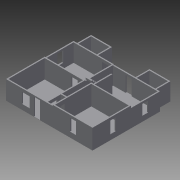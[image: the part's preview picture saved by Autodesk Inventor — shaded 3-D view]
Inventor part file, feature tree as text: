
AUTODESK INVENTOR PART (.ipt)
format: ipt  version: 2013 SP2 (Build 170200200, 200)  size: 604,672 bytes
history: native  units: in
note: dims shown in document units (in); Inventor stores cm internally (conversion verified against a paired STEP export)
features: extrude x20, sketch x13, projected_geometry x10, mirror x1
ambient origin geometry x8: Origin, YZ Plane, XZ Plane, XY Plane, X Axis, Y Axis, Z Axis, Center Point
feature tree (44):
  extrude  "Extrusion3"  Depth=18.0in
  extrude  "Extrusion4"  Depth=70.0in
  sketch  "Sketch4"  dims[d6=11.0in d8=70.0in d9=11.0in]
  extrude  "Extrusion5"  Depth=70.0in
  extrude  "Extrusion6"  Depth=6.0in
  extrude  "Extrusion7"  Depth=6.0in
  extrude  "Extrusion8"  Depth=6.0in
  extrude  "Extrusion9"  Depth=339.0in
  extrude  "Extrusion10"  Depth=182.0in
  extrude  "Extrusion11"  Depth=25.0in
  extrude  "Extrusion12"  Depth=30.0in
  extrude  "Extrusion13"  Depth=17.0in
  extrude  "Extrusion14"  Depth=25.0in
  extrude  "Extrusion15"  Depth=27.0in
  extrude  "Extrusion16"  Depth=6.0in
  extrude  "Extrusion21"  Depth=6.0in
  extrude  "Extrusion22"  Depth=39.0in
  mirror  "Mirror1"
  extrude  "Extrusion17"  Depth=138.0in
  extrude  "Extrusion18"  Depth=136.0in
  extrude  "Extrusion19"  Depth=175.0in
  extrude  "Extrusion20"  Depth=70.0in
  sketch  "Sketch1"  dims[d0=339.0in d2=434.0in d3=18.0in]
  sketch  "Sketch3"  dims[d4=398.0in d5=70.0in]
  projected_geometry  "Projected Loop2"
  projected_geometry  "Projected Loop3"
  projected_geometry  "Projected Loop4"
  projected_geometry  "Projected Loop5"
  projected_geometry  "Projected Loop6"
  projected_geometry  "Projected Loop7"
  sketch  "Sketch5"  dims[d10=6.0in d11=6.0in d12=6.0in d13=6.0in]
  projected_geometry  "Projected Loop8"
  sketch  "Sketch6"  dims[d14=6.0in d15=6.0in]
  projected_geometry  "Projected Loop9"
  sketch  "Sketch7"  dims[d16=6.0in d17=6.0in d18=339.0in]
  sketch  "Sketch8"  dims[d25=6.0in d26=339.0in]
  projected_geometry  "Projected Loop10"
  sketch  "Sketch9"  dims[d27=182.0in d28=193.0in d29=182.0in]
  sketch  "Sketch10"  dims[d32=138.0in d33=192.0in d34=25.0in d36=6.0in d37=182.0in]
  sketch  "Sketch11"  dims[d38=138.0in d39=208.0in d42=30.0in]
  projected_geometry  "Projected Loop11"
  sketch  "Sketch12"  dims[d43=6.0in d44=17.0in d45=49.0in]
  sketch  "Sketch13"  dims[d46=193.0in d47=6.0in d48=25.0in d49=16.0in]
  sketch  "Sketch14"  dims[d50=6.0in d54=27.0in d55=6.0in d56=6.0in d58=39.0in d59=138.0in d60=182.0in d61=136.0in d62=168.0in d63=175.0in d64=70.0in d65=39.0in d66=6.0in d67=139.0in d68=192.0in d69=6.0in d72=144.0in d75=263.0in d76=294.0in d77=25.0in d79=39.0in d80=6.0in d82=18.0in d83=39.0in d84=93.0in d85=93.0in d86=6.0in d87=6.0in d88=139.0in d89=6.0in d94=32.0in d95=33.0in d96=87.0in d97=0.0in d98=1.0in d99=0.0in d100=1.0in d101=0.0in d102=9.0in d103=0.0in d104=8.0in d105=0.0in d106=12.0in d107=0.0in d108=10.0in d109=0.0in d110=2.0in d111=0.0in d112=6.0in d113=0.0in d114=11.0in d115=0.0in d116=83.0in d118=13.0in d119=25.0in d123=25.0in d124=10.0in d125=11.0in d126=0.0in d127=76.0in d128=107.0in d129=25.0in d130=13.0in d133=25.0in d134=16.0in d135=11.0in d136=0.0in d137=52.0in d139=9.0in d140=26.0in d141=11.0in d142=0.0in d143=195.0in d144=7.5in d145=1.0in d146=8.0in d147=8.0in d148=7.5in d149=8.0in d150=7.5in d151=15.0in d152=8.0in d153=7.5in d154=8.0in d155=7.5in d156=15.0in d157=8.0in d158=7.5in d159=8.0in d160=7.5in d161=15.0in d162=8.0in d163=7.5in d164=8.0in d165=7.5in d166=15.0in d167=8.0in d168=7.5in d169=8.0in d170=7.5in d171=8.0in d172=7.5in d173=15.0in d174=8.0in d175=11.0in d176=0.0in d177=6.0in d178=0.0in d179=11.0in d180=0.0in d181=11.0in d182=0.0in d183=11.0in d184=0.0in d185=98.0in d186=26.0in d187=13.0in d188=72.0in d189=38.0in d190=1.0in d191=0.0in d192=28.0in d193=60.0in d194=28.0in d195=38.0in d196=80.0in d197=30.0in d198=20.0in d199=51.0in d200=17.0in d201=27.0in d202=1.0in d203=0.0in]
